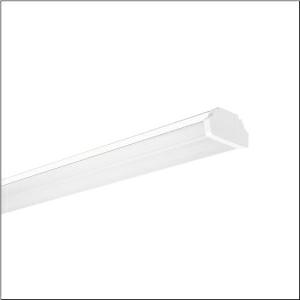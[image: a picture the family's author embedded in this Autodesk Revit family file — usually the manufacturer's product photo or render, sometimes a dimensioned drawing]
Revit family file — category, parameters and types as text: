
# Revit family: dus_31_gen_2_53bd8127v485c2_004c
name_source: partatom
category: Lighting Fixtures
units: mm (PartAtom-declared; Revit-internal decimal feet)

## family parameters
Cut with Voids When Loaded = No
Host = Face
Light Source = No
Part Type = Normal
Room Calculation Point = No
Round Connector Dimension = Use Diameter
Shared = No

## types (1)
- DUS 31 Gen.2 (1 x LED, 8590 lm, 47.9 W, 4000K)
    Apparent Load = 48 VA
    CIE Flux Codes = 47 80 95 93 100
    Color Rendering = 80
    Color Temperature = 4000K
    Default Elevation = 1800 mm
    Description = DUS 31 Gen.2, luminaire insert, of sheet steel, coil coated, white, length: 1.535mm, width: 81mm, height: 90mm, 5x system unit, system units: 307mm, LED rated luminous flux: 8.590lm, light colour: 840, SDCM (Standard Deviation of Colour Matching)MacAdam ≤ 3 SDCM (initial), control gear: ON/OFF, control gear: ECG, with plug, 3-pole, with phase selection, mains connection: 220..240V, AC, 50/60Hz, rated input power: 48W, through-wiring accessed according to module size, primary optical cover: cover, of PMMA, light emission: direct distribution, primary light characteristic: symmetric, protection rating (complete): IP20, protection rating (LED compartment): IP50, insulation class (complete): insulation class I (protective earthing), certification: CE, ENEC, VDE, UKCA, impact resistance: IK03, permissible ambient temperature for indoor applications: -35..+45°C, corresponds to IFS (International Featured Standards) requirements for safety and quality in the food industry, reducing of maximum allowable ambient temperature of 5°C with ceiling mounting, packaging unit: 1 piece
    Height = 95 mm
    Lamp = 1 x LED
    Lamp Light Flux = 8590 lm
    Lamp Power = 47.9 W
    Lamp count = 1
    Length = 1535 mm
    Luminous efficacy = 179 lm/W
    Manufacturer = Siteco
    ModVariant = No
    Model = 53BD8127V485C2
    Mounting Place = Ceiling
    Mounting Type = Pendant
    Number of Poles = 1
    OnlyDefault = Yes
    Power Factor = 1
    Product Name = DUS 31 Gen.2
    Product group = luminaire insert | ceiling pendant
    ProductGroupID = 901
    Protection Class = Protection class I
    Protection Degree = IP 20
    RLX_Detail_Level = 1
    RLX_Emergency_Light_Flux = 0 lm
    RLX_Emergency_Type = 0
    RLX_Emergency_Type_DB = No
    RlxData = <blob elided: 28533 chars, md5=6fc8870c>
    Socket = socket
    Standby Power = 0 W
    System Light Flux = 8590 lm
    System Power = 48 W
    Type Comments = Product without accessories
    Type Image = l_1319596.jpg
    URL = http://relux.com
    VarID = ---
    Voltage = 0 V
    Weight = 0.00 kg
    Width = 81 mm

## geometry (parser evidence)
native form markers: Blend x4, Sweep x12
no freeform markers — native parametric forms only
